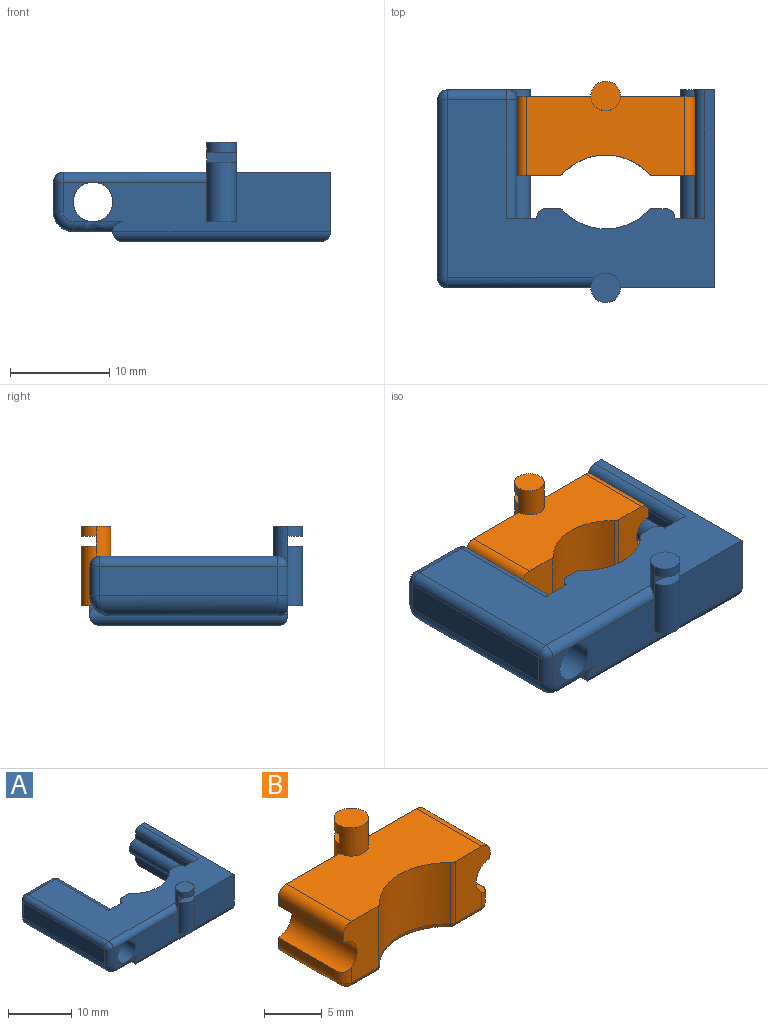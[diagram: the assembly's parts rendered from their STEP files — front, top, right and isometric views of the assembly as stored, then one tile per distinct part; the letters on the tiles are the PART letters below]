
ASSEMBLY  parts=2 mates=1
PART A: 64 faces, bbox 28.2x21.5x10 mm
  f0: plane 3x3mm, normal (0,1,0), area 3.9mm2, adj f47,f49,f53,f58
  f1: plane 24x6mm, normal (0,-1,0), area 109mm2, adj f2,f11,f12,f25,f41,f43,f47,f50
  f2: cylinder r=1.5mm len=6mm, axis (0,0,-1), area 28.3mm2, adj f1,f9,f11,f14
  f3: cylinder r=1.5mm len=3mm, axis (0,0,-1), area 4.7mm2, adj f9,f10,f15
  f4: plane 6.5x1.28mm, normal (0,1,0), area 8.3mm2, adj f12,f31,f33,f37
  f5: plane 4x3mm, normal (0,-1,0), area 5.5mm2, adj f47,f50,f51,f52,f62
  f6: plane 6.5x1.28mm, normal (0,1,0), area 8.3mm2, adj f12,f28,f29,f34
  f7: cylinder r=5.96mm len=8.71mm, axis (0,0,-1), area 63.5mm2, adj f12,f27,f28,f31
  f8: plane 20.02x18.02mm, normal (0,0,-1), area 136.6mm2, adj f16,f17,f18,f22,f27,f29,f33,f36
  f9: cylinder r=1.5mm len=4mm, axis (0,0,-1), area 14.5mm2, adj f2,f3,f10,f12,f13,f62
  f10: plane 3x2.98mm, normal (0,0,1), area 7mm2, adj f3,f9
  f11: plane 3x1.5mm, normal (0,0,-1), area 3.5mm2, adj f1,f2
  f12: plane 27x20mm, normal (0,0,1), area 256.7mm2, adj f1,f4,f6,f7,f9,f16,f17,f25
  f13: plane 3x1mm, normal (0,-1,0), area 3mm2, adj f9,f14,f15
  f14: plane 3x1.5mm, normal (0,0,1), area 3.5mm2, adj f2,f13
  f15: plane 3x1.5mm, normal (0,0,-1), area 3.5mm2, adj f3,f13
  f16: plane 7x4mm, normal (0,1,0), area 11.4mm2, adj f8,f12,f18,f19,f20,f34,f36,f56
  f17: plane 7x4mm, normal (0,1,0), area 11.4mm2, adj f8,f12,f22,f23,f24,f37,f39,f63
  f18: plane 13x2.1mm, normal (1,0,0), area 26.9mm2, adj f8,f16,f20,f40,f49
  f19: plane 12x1.1mm, normal (1,0,0), area 13.2mm2, adj f16,f20,f55,f56
  f20: cylinder r=1.4mm len=13mm, axis (0,-1,0), area 57.6mm2, adj f16,f18,f19,f21,f49,f55
  f21: plane 5.4x3mm, normal (0,1,0), area 7.9mm2, adj f20,f47,f49,f55,f58
  f22: plane 13x2.1mm, normal (-1,0,0), area 27.1mm2, adj f8,f17,f24,f26,f42
  f23: plane 13x1.1mm, normal (-1,0,0), area 14.3mm2, adj f17,f24,f26,f63
  f24: cylinder r=1.4mm len=13mm, axis (0,-1,0), area 57.2mm2, adj f17,f22,f23,f26
  f25: plane 20x6mm, normal (1,0,0), area 120mm2, adj f1,f12,f26,f44
  f26: plane 6x3.4mm, normal (0,1,0), area 14.9mm2, adj f12,f22,f23,f24,f25,f42,f63
  f27: bspline ~9.45x2.39mm, area 8.2mm2, adj f7,f8,f30,f32
  f28: cylinder r=0.5mm len=6.5mm, axis (0,0,-1), area 2.7mm2, adj f6,f7,f12,f30
  f29: cylinder r=0.5mm len=1.28mm, axis (1,0,0), area 1mm2, adj f6,f8,f30,f35
  f30: bspline ~0.5x0.5mm, area 0.2mm2, adj f27,f28,f29
  f31: cylinder r=0.5mm len=6.5mm, axis (0,0,-1), area 2.7mm2, adj f4,f7,f12,f32
  f32: bspline ~0.5x0.5mm, area 0.2mm2, adj f27,f31,f33
  f33: cylinder r=0.5mm len=1.28mm, axis (1,0,0), area 1mm2, adj f4,f8,f32,f38
  f34: cylinder r=1mm len=6.5mm, axis (0,0,-1), area 9.8mm2, adj f6,f12,f16,f35
  f35: bspline ~1.19x1mm, area 0.5mm2, adj f29,f34,f36
  f36: cylinder r=1mm len=1mm, axis (0,1,0), area 0.4mm2, adj f8,f16,f35
  f37: cylinder r=1mm len=6.5mm, axis (0,0,-1), area 9.8mm2, adj f4,f12,f17,f38
  f38: bspline ~1.19x1mm, area 0.5mm2, adj f33,f37,f39
  f39: cylinder r=1mm len=1mm, axis (0,-1,0), area 0.4mm2, adj f8,f17,f38
  f40: cylinder r=1mm len=2mm, axis (-1,0,0), area 4.3mm2, adj f8,f18,f41,f49
  f41: cylinder r=1mm len=19.6mm, axis (0,1,0), area 30.8mm2, adj f1,f8,f40,f43,f45,f49,f50
  f42: cylinder r=1mm len=2mm, axis (1,0,0), area 2.4mm2, adj f8,f22,f26,f44
  f43: cylinder r=1mm len=22mm, axis (-1,0,0), area 33mm2, adj f1,f8,f41,f44
  f44: cylinder r=1mm len=20mm, axis (0,-1,0), area 29.8mm2, adj f8,f25,f42,f43
  f45: plane 17x4mm, normal (0,0,-1), area 68mm2, adj f41,f48,f49,f50
  f46: plane 18x3mm, normal (-1,0,0), area 54mm2, adj f48,f52,f53,f60
  f47: cylinder r=2mm len=20mm, axis (0,1,0), area 251.3mm2, adj f0,f1,f5,f21,f49
  f48: cylinder r=2mm len=18mm, axis (0,1,0), area 55mm2, adj f45,f46,f51,f54
  f49: cylinder r=2mm len=8.31mm, axis (1,0,0), area 15.6mm2, adj f0,f18,f20,f21,f40,f41,f45,f47
  f50: cylinder r=1mm len=5mm, axis (-1,0,0), area 7.1mm2, adj f1,f5,f41,f45,f51
  f51: torus R=1mm, axis (0,-1,0), area 4mm2, adj f5,f48,f50,f52
  f52: cylinder r=1mm len=3mm, axis (0,0,-1), area 4.7mm2, adj f5,f46,f51,f61
  f53: cylinder r=1mm len=3mm, axis (0,0,1), area 4.7mm2, adj f0,f46,f54,f59
  f54: bspline ~2.1x2mm, area 2.2mm2, adj f48,f49,f53
  f55: cylinder r=1mm len=1.52mm, axis (0,0,-1), area 2.1mm2, adj f19,f20,f21,f57
  f56: cylinder r=1mm len=12mm, axis (0,1,0), area 18.8mm2, adj f12,f16,f19,f57
  f57: sphere r=1mm, area 1mm2, adj f55,f56,f58
  f58: cylinder r=1mm len=6mm, axis (1,0,0), area 9.4mm2, adj f0,f12,f21,f57,f59
  f59: sphere r=1mm, area 2.1mm2, adj f53,f58,f60
  f60: cylinder r=1mm len=18mm, axis (0,-1,0), area 28.3mm2, adj f12,f46,f59,f61
  f61: sphere r=1mm, area 1.6mm2, adj f52,f60,f62
  f62: cylinder r=1mm len=14.9mm, axis (1,0,0), area 23.1mm2, adj f1,f5,f9,f12,f61
  f63: cylinder r=1mm len=13mm, axis (0,-1,0), area 20.4mm2, adj f12,f17,f23,f26
PART B: 36 faces, bbox 18x9.5x10 mm
  f0: plane 7x0.8mm, normal (-1,0,0), area 5.6mm2, adj f3,f19,f31,f33
  f1: plane 8x0.8mm, normal (1,0,0), area 6.4mm2, adj f2,f3,f18,f34
  f2: plane 6.5x4.28mm, normal (0,-1,0), area 21.6mm2, adj f1,f12,f18,f24,f26,f27,f34
  f3: plane 18x6mm, normal (0,1,0), area 83.5mm2, adj f0,f1,f5,f11,f12,f16,f17,f18
  f4: plane 6.5x4.28mm, normal (0,-1,0), area 21.6mm2, adj f12,f16,f19,f21,f23,f33,f35
  f5: cylinder r=1.5mm len=6mm, axis (0,0,-1), area 28.3mm2, adj f3,f9,f11,f14
  f6: cylinder r=1.5mm len=3mm, axis (0,0,-1), area 4.7mm2, adj f9,f10,f15
  f7: cylinder r=5.96mm len=8.71mm, axis (0,0,-1), area 63.5mm2, adj f12,f20,f21,f24
  f8: plane 16.02x6.58mm, normal (0,0,-1), area 90.6mm2, adj f20,f23,f26,f29,f30,f31
  f9: cylinder r=1.5mm len=3mm, axis (0,0,-1), area 14mm2, adj f5,f6,f10,f12,f13
  f10: plane 3x2.98mm, normal (0,0,1), area 7mm2, adj f6,f9
  f11: plane 3x1.5mm, normal (0,0,-1), area 3.5mm2, adj f3,f5
  f12: plane 16x8mm, normal (0,0,1), area 111.7mm2, adj f2,f3,f4,f7,f9,f21,f24,f34
  f13: plane 3x1mm, normal (0,1,0), area 3mm2, adj f9,f14,f15
  f14: plane 3x1.5mm, normal (0,0,1), area 3.5mm2, adj f5,f13
  f15: plane 3x1.5mm, normal (0,0,-1), area 3.5mm2, adj f6,f13
  f16: plane 8x0.8mm, normal (-1,0,0), area 6.4mm2, adj f3,f4,f19,f35
  f17: plane 7x0.8mm, normal (1,0,0), area 5.6mm2, adj f3,f18,f27,f29
  f18: cylinder r=1.7mm len=8mm, axis (0,1,0), area 42.2mm2, adj f1,f2,f3,f17,f27
  f19: cylinder r=1.7mm len=8mm, axis (0,1,0), area 42.2mm2, adj f0,f3,f4,f16,f33
  f20: bspline ~9.45x2.39mm, area 8.2mm2, adj f7,f8,f22,f25
  f21: cylinder r=0.5mm len=6.5mm, axis (0,0,-1), area 2.7mm2, adj f4,f7,f12,f22
  f22: bspline ~0.5x0.5mm, area 0.2mm2, adj f20,f21,f23
  f23: cylinder r=0.5mm len=3.28mm, axis (1,0,0), area 2.6mm2, adj f4,f8,f22,f32
  f24: cylinder r=0.5mm len=6.5mm, axis (0,0,-1), area 2.7mm2, adj f2,f7,f12,f25
  f25: bspline ~0.5x0.5mm, area 0.2mm2, adj f20,f24,f26
  f26: cylinder r=0.5mm len=3.28mm, axis (1,0,0), area 2.6mm2, adj f2,f8,f25,f28
  f27: cylinder r=1mm len=1.63mm, axis (0,0,-1), area 1.9mm2, adj f2,f17,f18,f28
  f28: bspline ~1.05x1mm, area 0.5mm2, adj f26,f27,f29
  f29: cylinder r=1mm len=7.5mm, axis (0,1,0), area 10.6mm2, adj f8,f17,f28,f30
  f30: cylinder r=1mm len=18mm, axis (-1,0,0), area 26.7mm2, adj f3,f8,f29,f31
  f31: cylinder r=1mm len=7.5mm, axis (0,-1,0), area 10.6mm2, adj f0,f8,f30,f32
  f32: bspline ~1.19x1mm, area 0.5mm2, adj f23,f31,f33
  f33: cylinder r=1mm len=1.63mm, axis (0,0,-1), area 1.9mm2, adj f0,f4,f19,f32
  f34: cylinder r=1mm len=8mm, axis (0,-1,0), area 12.6mm2, adj f1,f2,f3,f12
  f35: cylinder r=1mm len=8mm, axis (0,1,0), area 12.6mm2, adj f3,f4,f12,f16
PLACE A t=(-1.84,-3.56,-4.4)mm fixed
PLACE B t=(-1.84,-0.2,-4.4)mm
MATE slider A.f20 <-> B.f19  axis (0,1,0) through (-10.84,8.44,-0.9)mm
